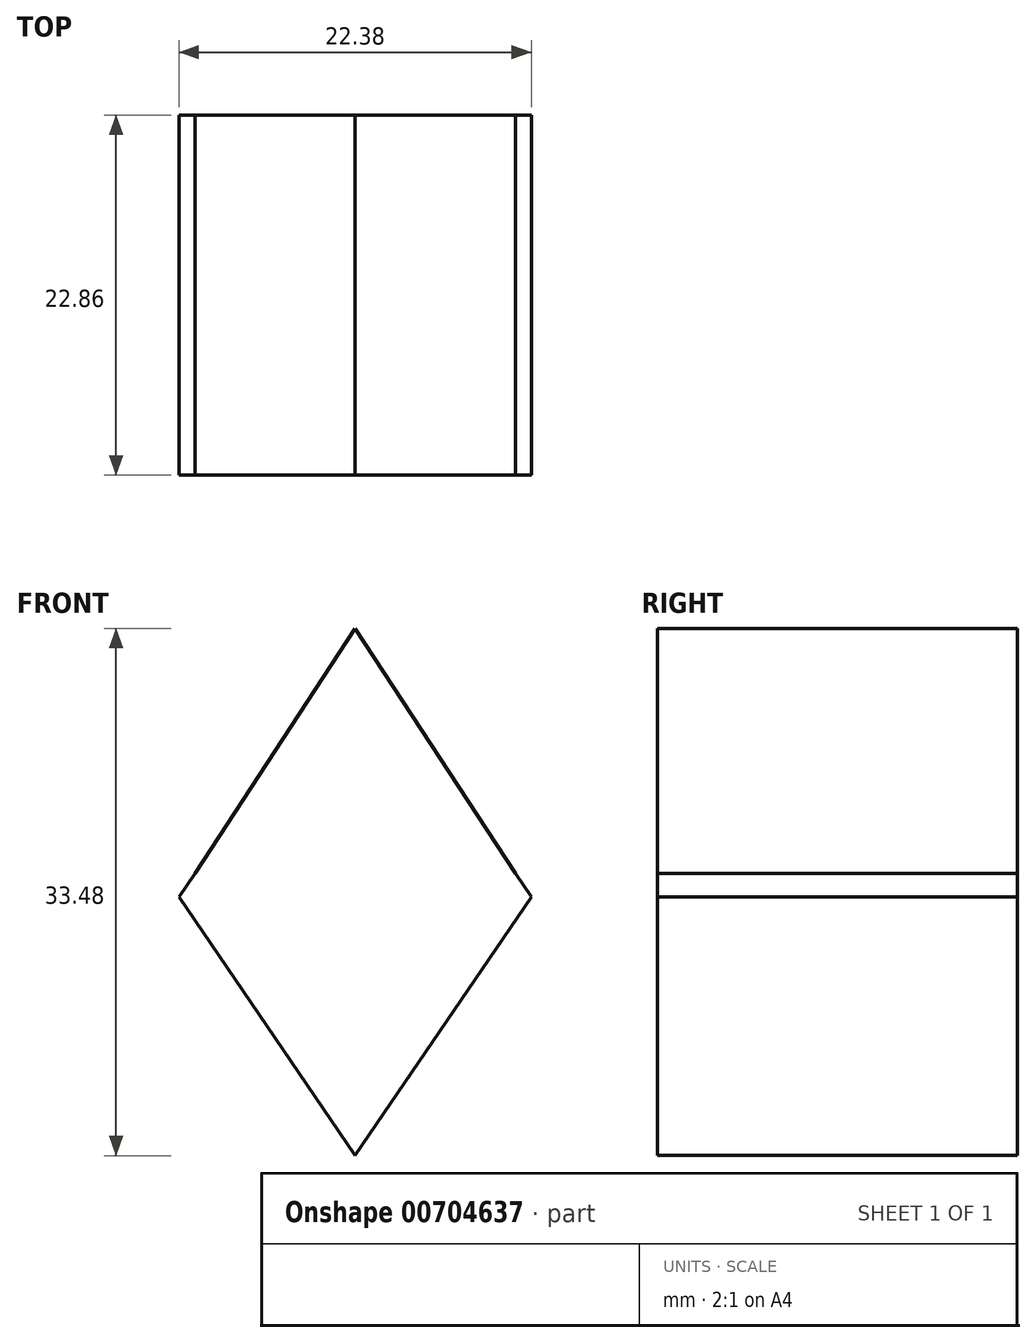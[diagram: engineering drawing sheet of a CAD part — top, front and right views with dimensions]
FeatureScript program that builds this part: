
annotation { "Feature Type Name" : "Feature", "Feature Type Description" : "" }
export const myFeature = defineFeature(function(context is Context, id is Id, definition is map)
    precondition{}
    {
        {
            var Q0;
            Q0=qCreatedBy(makeId("Front.planeOp"),FACE);
            var sketch = newSketch(context, id + "F0", { "sketchPlane" : qUnion([Q0])});
            skFitSpline(sketch, "E0", {"points": [v(-18.66, -145.03) * mm, v(-12.41, -140.25) * mm, v(-7.43, -132.73) * mm], "startDerivative": vector(13.73, 8.78) * mm, "endDerivative": vector(8.77, 15.73) * mm});
            skFitSpline(sketch, "E1", {"points": [v(0, -156.5) * mm, v(-5.42, -154.99) * mm, v(-8.85, -151.2) * mm], "startDerivative": vector(-11.5, 1.7) * mm, "endDerivative": vector(-6.16, 8.95) * mm});
            skFitSpline(sketch, "E2", {"points": [v(-6.32, -27.2) * mm, v(-15.28, -19.21) * mm, v(-26.43, -12.1) * mm, v(-37.33, -8.05) * mm], "startDerivative": vector(-25.96, 24.63) * mm, "endDerivative": vector(-33.62, 10.63) * mm});
            skFitSpline(sketch, "E3", {"points": [v(-37.33, -3.8) * mm, v(-39.84, -2.96) * mm, v(-42.51, -2.04) * mm, v(-42.5, -2) * mm], "startDerivative": vector(-4.66, 1.6) * mm, "endDerivative": vector(0.46, 0.6) * mm});
            skFitSpline(sketch, "E4", {"points": [v(-42.5, -2) * mm, v(-36.56, 4.25) * mm, v(-31.56, 12.84) * mm], "startDerivative": vector(12.98, 12.08) * mm, "endDerivative": vector(8.97, 17.54) * mm});
            skFitSpline(sketch, "E5", {"points": [v(-31.56, 12.84) * mm, v(-28.75, 11.67) * mm, v(-26.43, 10.32) * mm], "startDerivative": vector(5.62, -2.14) * mm, "endDerivative": vector(4.63, -2.93) * mm});
            skFitSpline(sketch, "E6", {"points": [v(-23.95, 12.84) * mm, v(-17.54, 8.59) * mm, v(-10.17, 1.5) * mm], "startDerivative": vector(13.82, -8.22) * mm, "endDerivative": vector(13.74, -14.33) * mm});
            skLineSegment(sketch, "E7", {"start": v(-10.17, 1.5) * mm, "end": v(0, 17.06) * mm});
            skLineSegment(sketch, "E8", {"start": v(0, 17.06) * mm, "end": v(0, 9.54) * mm});
            skLineSegment(sketch, "E9", {"start": v(0, 9.54) * mm, "end": v(0, 17.06) * mm});
            skLineSegment(sketch, "E10", {"start": v(-37.33, -3.8) * mm, "end": v(-37.33, -8.05) * mm});
            skLineSegment(sketch, "E11", {"start": v(-23.95, 12.84) * mm, "end": v(-26.43, 10.32) * mm});
            skLineSegment(sketch, "E12", {"start": v(-6.32, -27.2) * mm, "end": v(0, -29.82) * mm});
            skLineSegment(sketch, "E13", {"start": v(0, -29.82) * mm, "end": v(-6.32, -27.2) * mm});
            skLineSegment(sketch, "E14", {"start": v(-7.43, -132.73) * mm, "end": v(-4.54, -130.41) * mm});
            skLineSegment(sketch, "E15", {"start": v(-4.54, -130.41) * mm, "end": v(0, -130.41) * mm});
            skLineSegment(sketch, "E16", {"start": v(0, -130.41) * mm, "end": v(-4.54, -130.41) * mm});
            skLineSegment(sketch, "E17", {"start": v(-8.85, -151.2) * mm, "end": v(-10.72, -152.9) * mm});
            skLineSegment(sketch, "E18", {"start": v(-10.72, -152.9) * mm, "end": v(-18.24, -148.4) * mm});
            skLineSegment(sketch, "E19", {"start": v(-18.24, -148.4) * mm, "end": v(-18.66, -145.03) * mm});
            skLineSegment(sketch, "E20.MirrorCS", {"start": v(10.17, 1.5) * mm, "end": v(0, 17.06) * mm});
            skFitSpline(sketch, "E21.MirrorCS", {"points": [v(23.95, 12.84) * mm, v(17.54, 8.59) * mm, v(10.17, 1.5) * mm], "startDerivative": vector(-13.82, -8.22) * mm, "endDerivative": vector(-13.74, -14.33) * mm});
            skLineSegment(sketch, "E22.MirrorCS", {"start": v(23.95, 12.84) * mm, "end": v(26.43, 10.32) * mm});
            skFitSpline(sketch, "E23.MirrorCS", {"points": [v(31.56, 12.84) * mm, v(28.75, 11.67) * mm, v(26.43, 10.32) * mm], "startDerivative": vector(-5.62, -2.14) * mm, "endDerivative": vector(-4.63, -2.93) * mm});
            skFitSpline(sketch, "E24.MirrorCS", {"points": [v(42.5, -2) * mm, v(36.56, 4.25) * mm, v(31.56, 12.84) * mm], "startDerivative": vector(-12.98, 12.08) * mm, "endDerivative": vector(-8.97, 17.54) * mm});
            skFitSpline(sketch, "E25.MirrorCS", {"points": [v(37.33, -3.8) * mm, v(39.84, -2.96) * mm, v(42.51, -2.04) * mm, v(42.5, -2) * mm], "startDerivative": vector(4.66, 1.6) * mm, "endDerivative": vector(-0.46, 0.6) * mm});
            skLineSegment(sketch, "E26.MirrorCS", {"start": v(37.33, -3.8) * mm, "end": v(37.33, -8.05) * mm});
            skFitSpline(sketch, "E27.MirrorCS", {"points": [v(6.32, -27.2) * mm, v(15.28, -19.21) * mm, v(26.43, -12.1) * mm, v(37.33, -8.05) * mm], "startDerivative": vector(25.96, 24.63) * mm, "endDerivative": vector(33.62, 10.63) * mm});
            skLineSegment(sketch, "E28.MirrorCS", {"start": v(6.32, -27.2) * mm, "end": v(0, -29.82) * mm});
            skLineSegment(sketch, "E29.MirrorCS", {"start": v(0, -130.41) * mm, "end": v(4.54, -130.41) * mm});
            skLineSegment(sketch, "E30.MirrorCS", {"start": v(7.43, -132.73) * mm, "end": v(4.54, -130.41) * mm});
            skFitSpline(sketch, "E31.MirrorCS", {"points": [v(18.66, -145.03) * mm, v(12.41, -140.25) * mm, v(7.43, -132.73) * mm], "startDerivative": vector(-13.73, 8.78) * mm, "endDerivative": vector(-8.77, 15.73) * mm});
            skLineSegment(sketch, "E32.MirrorCS", {"start": v(18.24, -148.4) * mm, "end": v(18.66, -145.03) * mm});
            skLineSegment(sketch, "E33.MirrorCS", {"start": v(10.72, -152.9) * mm, "end": v(18.24, -148.4) * mm});
            skLineSegment(sketch, "E34.MirrorCS", {"start": v(8.85, -151.2) * mm, "end": v(10.72, -152.9) * mm});
            skFitSpline(sketch, "E35.MirrorCS", {"points": [v(0, -156.5) * mm, v(5.42, -154.99) * mm, v(8.85, -151.2) * mm], "startDerivative": vector(11.5, 1.7) * mm, "endDerivative": vector(6.16, 8.95) * mm});
            skSolve(sketch);
        }
        {
            var Q0;
            Q0=makeQuery(id+"F0.imprint","IMPRINT",FACE,{"disambiguationData":[TD([[makeQuery(id+"F0.imprint","IMPRINT",EDGE,{"derivedFrom":sQuery(id+"F0.wireOp",EDGE,"E2")}),-1.0]])]});
            var Q1;
            Q1=makeQuery(id+"F0.imprint","IMPRINT",FACE,{"disambiguationData":[TD([[makeQuery(id+"F0.imprint","IMPRINT",EDGE,{"derivedFrom":sQuery(id+"F0.wireOp",EDGE,"E0")}),-1.0]])]});
            extrude(context, id + "F1", {"entities" : qUnion([Q0, Q1]), "depth" : 6.35 * mm, "offsetDistance" : 25.4 * mm});
        }
        {
            var Q0;
            Q0=makeQuery(id+"F1.opExtrude","CAP_FACE",FACE,{"disambiguationData":[OSD([sQuery(id+"F0.wireOp",EDGE,"E2"),sQuery(id+"F0.wireOp",EDGE,"E3"),sQuery(id+"F0.wireOp",EDGE,"E4"),sQuery(id+"F0.wireOp",EDGE,"E5"),sQuery(id+"F0.wireOp",EDGE,"E6"),sQuery(id+"F0.wireOp",EDGE,"E7"),sQuery(id+"F0.wireOp",EDGE,"E10"),sQuery(id+"F0.wireOp",EDGE,"E11"),sQuery(id+"F0.wireOp",EDGE,"E13"),sQuery(id+"F0.wireOp",EDGE,"E20.MirrorCS"),sQuery(id+"F0.wireOp",EDGE,"E21.MirrorCS"),sQuery(id+"F0.wireOp",EDGE,"E22.MirrorCS"),sQuery(id+"F0.wireOp",EDGE,"E23.MirrorCS"),sQuery(id+"F0.wireOp",EDGE,"E24.MirrorCS"),sQuery(id+"F0.wireOp",EDGE,"E25.MirrorCS"),sQuery(id+"F0.wireOp",EDGE,"E26.MirrorCS"),sQuery(id+"F0.wireOp",EDGE,"E27.MirrorCS"),sQuery(id+"F0.wireOp",EDGE,"E28.MirrorCS")])],"isStart":true});
            var Q1;
            Q1=makeQuery(id+"F1.opExtrude","CAP_FACE",FACE,{"disambiguationData":[OSD([sQuery(id+"F0.wireOp",EDGE,"E0"),sQuery(id+"F0.wireOp",EDGE,"E1"),sQuery(id+"F0.wireOp",EDGE,"E14"),sQuery(id+"F0.wireOp",EDGE,"E16"),sQuery(id+"F0.wireOp",EDGE,"E17"),sQuery(id+"F0.wireOp",EDGE,"E18"),sQuery(id+"F0.wireOp",EDGE,"E19"),sQuery(id+"F0.wireOp",EDGE,"E29.MirrorCS"),sQuery(id+"F0.wireOp",EDGE,"E30.MirrorCS"),sQuery(id+"F0.wireOp",EDGE,"E31.MirrorCS"),sQuery(id+"F0.wireOp",EDGE,"E32.MirrorCS"),sQuery(id+"F0.wireOp",EDGE,"E33.MirrorCS"),sQuery(id+"F0.wireOp",EDGE,"E34.MirrorCS"),sQuery(id+"F0.wireOp",EDGE,"E35.MirrorCS")])],"isStart":true});
            extrude(context, id + "F2", {"entities" : qUnion([Q0, Q1]), "depth" : 6.35 * mm, "offsetDistance" : 25.4 * mm});
        }
        {
            var Q0;
            Q0=makeQuery(id+"F1.opExtrude","CAP_FACE",FACE,{"disambiguationData":[OSD([sQuery(id+"F0.wireOp",EDGE,"E2"),sQuery(id+"F0.wireOp",EDGE,"E3"),sQuery(id+"F0.wireOp",EDGE,"E4"),sQuery(id+"F0.wireOp",EDGE,"E5"),sQuery(id+"F0.wireOp",EDGE,"E6"),sQuery(id+"F0.wireOp",EDGE,"E7"),sQuery(id+"F0.wireOp",EDGE,"E10"),sQuery(id+"F0.wireOp",EDGE,"E11"),sQuery(id+"F0.wireOp",EDGE,"E13"),sQuery(id+"F0.wireOp",EDGE,"E20.MirrorCS"),sQuery(id+"F0.wireOp",EDGE,"E21.MirrorCS"),sQuery(id+"F0.wireOp",EDGE,"E22.MirrorCS"),sQuery(id+"F0.wireOp",EDGE,"E23.MirrorCS"),sQuery(id+"F0.wireOp",EDGE,"E24.MirrorCS"),sQuery(id+"F0.wireOp",EDGE,"E25.MirrorCS"),sQuery(id+"F0.wireOp",EDGE,"E26.MirrorCS"),sQuery(id+"F0.wireOp",EDGE,"E27.MirrorCS"),sQuery(id+"F0.wireOp",EDGE,"E28.MirrorCS")])],"isStart":false});
            var sketch = newSketch(context, id + "F3", { "sketchPlane" : qUnion([Q0])});
            skFitSpline(sketch, "E36", {"points": [v(-26.43, 10.32) * mm, v(-20.88, 7.37) * mm, v(-15.82, 3.86) * mm, v(-11.19, 0) * mm, v(-9.86, -1.24) * mm], "startDerivative": vector(19.99, -10.01) * mm, "endDerivative": vector(7.2, -6.92) * mm});
            skLineSegment(sketch, "E37", {"start": v(-9.86, -1.24) * mm, "end": v(0, -16.46) * mm});
            skLineSegment(sketch, "E38.MirrorCS", {"start": v(9.86, -1.24) * mm, "end": v(0, -16.46) * mm});
            skFitSpline(sketch, "E39.MirrorCS", {"points": [v(26.43, 10.32) * mm, v(20.88, 7.37) * mm, v(15.82, 3.86) * mm, v(11.19, 0) * mm, v(9.86, -1.24) * mm], "startDerivative": vector(-19.99, -10.01) * mm, "endDerivative": vector(-7.2, -6.92) * mm});
            skLineSegment(sketch, "E40", {"start": v(-10.17, 1.5) * mm, "end": v(-11.19, 0) * mm});
            skLineSegment(sketch, "E41", {"start": v(10.17, 1.5) * mm, "end": v(11.19, 0) * mm});
            skSolve(sketch);
        }
        {
            var Q0;
            {var subQ7=sQuery(id+"F3.wireOp",EDGE,"E37");Q0=makeQuery(id+"F3.imprint","IMPRINT",FACE,{"disambiguationData":[TD([[makeQuery(id+"F3.imprint","IMPRINT",EDGE,{"derivedFrom":subQ7}),-1.0]])]});}
            var Q1;
            {var subQ3=sQuery(id+"F3.wireOp",EDGE,"E37");Q1=makeQuery(id+"F3.imprint","IMPRINT",FACE,{"disambiguationData":[TD([[makeQuery(id+"F3.imprint","IMPRINT",EDGE,{"derivedFrom":subQ3}),1.0]])]});}
            extrude(context, id + "F4", {"entities" : qUnion([Q0, Q1]), "operationType" : NewBodyOperationType.ADD, "depth" : 2.54 * mm, "offsetDistance" : 25.4 * mm});
        }
        {
            var Q0;
            Q0=makeQuery(id+"F4.opExtrude","CAP_FACE",FACE,{"disambiguationData":[OSD([sQuery(id+"F0.wireOp",EDGE,"E2"),sQuery(id+"F0.wireOp",EDGE,"E3"),sQuery(id+"F0.wireOp",EDGE,"E4"),sQuery(id+"F0.wireOp",EDGE,"E5"),sQuery(id+"F0.wireOp",EDGE,"E7"),sQuery(id+"F0.wireOp",EDGE,"E10"),sQuery(id+"F0.wireOp",EDGE,"E13"),sQuery(id+"F0.wireOp",EDGE,"E20.MirrorCS"),sQuery(id+"F0.wireOp",EDGE,"E23.MirrorCS"),sQuery(id+"F0.wireOp",EDGE,"E24.MirrorCS"),sQuery(id+"F0.wireOp",EDGE,"E25.MirrorCS"),sQuery(id+"F0.wireOp",EDGE,"E26.MirrorCS"),sQuery(id+"F0.wireOp",EDGE,"E27.MirrorCS"),sQuery(id+"F0.wireOp",EDGE,"E28.MirrorCS"),sQuery(id+"F3.wireOp",EDGE,"E36"),sQuery(id+"F3.wireOp",EDGE,"E39.MirrorCS"),sQuery(id+"F3.wireOp",EDGE,"E40"),sQuery(id+"F3.wireOp",EDGE,"E41")])],"isStart":false});
            extrude(context, id + "F5", {"entities" : qUnion([Q0]), "oppositeDirection" : true, "depth" : 17.78 * mm, "offsetDistance" : 25.4 * mm});
        }
        {
            var Q0;
            Q0=makeQuery(id+"F5.opExtrude","CAP_FACE",FACE,{"disambiguationData":[OSD([sQuery(id+"F0.wireOp",EDGE,"E2"),sQuery(id+"F0.wireOp",EDGE,"E3"),sQuery(id+"F0.wireOp",EDGE,"E4"),sQuery(id+"F0.wireOp",EDGE,"E5"),sQuery(id+"F0.wireOp",EDGE,"E7"),sQuery(id+"F0.wireOp",EDGE,"E10"),sQuery(id+"F0.wireOp",EDGE,"E13"),sQuery(id+"F0.wireOp",EDGE,"E20.MirrorCS"),sQuery(id+"F0.wireOp",EDGE,"E23.MirrorCS"),sQuery(id+"F0.wireOp",EDGE,"E24.MirrorCS"),sQuery(id+"F0.wireOp",EDGE,"E25.MirrorCS"),sQuery(id+"F0.wireOp",EDGE,"E26.MirrorCS"),sQuery(id+"F0.wireOp",EDGE,"E27.MirrorCS"),sQuery(id+"F0.wireOp",EDGE,"E28.MirrorCS"),sQuery(id+"F3.wireOp",EDGE,"E36"),sQuery(id+"F3.wireOp",EDGE,"E39.MirrorCS"),sQuery(id+"F3.wireOp",EDGE,"E40"),sQuery(id+"F3.wireOp",EDGE,"E41")])],"isStart":true});
            var sketch = newSketch(context, id + "F6", { "sketchPlane" : qUnion([Q0])});
            skLineSegment(sketch, "E42", {"start": v(-11.19, 0) * mm, "end": v(0, -16.42) * mm});
            skLineSegment(sketch, "E43", {"start": v(0, -16.42) * mm, "end": v(11.19, 0) * mm});
            skSolve(sketch);
        }
        {
            var Q0;
            Q0=makeQuery(id+"F6.imprint","IMPRINT",FACE,{"disambiguationData":[TD([[makeQuery(id+"F6.imprint","IMPRINT",EDGE,{"derivedFrom":sQuery(id+"F6.wireOp",EDGE,"E42")}),-1.0]])]});
            var sketch = newSketch(context, id + "F7", { "sketchPlane" : qUnion([Q0])});
            skLineSegment(sketch, "E44", {"start": v(0, -16.57) * mm, "end": v(-11.35, 0) * mm});
            skLineSegment(sketch, "E45", {"start": v(-11.35, 0) * mm, "end": v(0, -16.57) * mm});
            skLineSegment(sketch, "E46.MirrorCS", {"start": v(11.35, 0) * mm, "end": v(0, -16.57) * mm});
            skSolve(sketch);
        }
        {
            var Q0;
            Q0=makeQuery(id+"F6.imprint","IMPRINT",FACE,{"disambiguationData":[TD([[makeQuery(id+"F6.imprint","IMPRINT",EDGE,{"derivedFrom":sQuery(id+"F6.wireOp",EDGE,"E42")}),1.0]])]});
            extrude(context, id + "F8", {"entities" : qUnion([Q0]), "operationType" : NewBodyOperationType.ADD, "depth" : 2.54 * mm, "offsetDistance" : 25.4 * mm});
        }
        {
            var Q0;
            Q0=makeQuery(id+"F8.opExtrude","CAP_FACE",FACE,{"disambiguationData":[OSD([sQuery(id+"F0.wireOp",EDGE,"E7"),sQuery(id+"F0.wireOp",EDGE,"E20.MirrorCS"),sQuery(id+"F3.wireOp",EDGE,"E40"),sQuery(id+"F3.wireOp",EDGE,"E41"),sQuery(id+"F6.wireOp",EDGE,"E42"),sQuery(id+"F6.wireOp",EDGE,"E43")])],"isStart":false});
            extrude(context, id + "F9", {"entities" : qUnion([Q0]), "operationType" : NewBodyOperationType.ADD, "oppositeDirection" : true, "depth" : 22.86 * mm, "offsetDistance" : 25.4 * mm});
        }
        {
            var Q0;
            Q0=makeQuery(id+"F7.imprint","IMPRINT",FACE,{"disambiguationData":[TD([[makeQuery(id+"F7.imprint","IMPRINT",EDGE,{"derivedFrom":makeQuery(id+"F6.imprint","IMPRINT",EDGE,{"derivedFrom":sQuery(id+"F6.wireOp",EDGE,"E42")})}),-1.0]])]});
            var Q1;
            {var subQ0=sQuery(id+"F0.wireOp",EDGE,"E11");var subQ1=sQuery(id+"F0.wireOp",EDGE,"E7");var subQ2=sQuery(id+"F0.wireOp",EDGE,"E6");var subQ3=sQuery(id+"F0.wireOp",EDGE,"E5");Q1=makeQuery(id+"F4.boolean.opBoolean","SPLIT",FACE,{"disambiguationData":[TD([makeQuery(id+"F1.opExtrude","SWEPT_FACE",FACE,{"disambiguationData":[OSD([subQ3])]})])],"derivedFrom":makeQuery(id+"F1.opExtrude","CAP_FACE",FACE,{"disambiguationData":[OSD([sQuery(id+"F0.wireOp",EDGE,"E2"),sQuery(id+"F0.wireOp",EDGE,"E3"),sQuery(id+"F0.wireOp",EDGE,"E4"),subQ3,subQ2,subQ1,sQuery(id+"F0.wireOp",EDGE,"E10"),subQ0,sQuery(id+"F0.wireOp",EDGE,"E13"),sQuery(id+"F0.wireOp",EDGE,"E20.MirrorCS"),sQuery(id+"F0.wireOp",EDGE,"E21.MirrorCS"),sQuery(id+"F0.wireOp",EDGE,"E22.MirrorCS"),sQuery(id+"F0.wireOp",EDGE,"E23.MirrorCS"),sQuery(id+"F0.wireOp",EDGE,"E24.MirrorCS"),sQuery(id+"F0.wireOp",EDGE,"E25.MirrorCS"),sQuery(id+"F0.wireOp",EDGE,"E26.MirrorCS"),sQuery(id+"F0.wireOp",EDGE,"E27.MirrorCS"),sQuery(id+"F0.wireOp",EDGE,"E28.MirrorCS")])],"isStart":false})});}
            var Q2;
            {var subQ0=sQuery(id+"F0.wireOp",EDGE,"E23.MirrorCS");var subQ1=sQuery(id+"F0.wireOp",EDGE,"E22.MirrorCS");var subQ2=sQuery(id+"F0.wireOp",EDGE,"E21.MirrorCS");var subQ3=sQuery(id+"F0.wireOp",EDGE,"E20.MirrorCS");Q2=makeQuery(id+"F4.boolean.opBoolean","SPLIT",FACE,{"disambiguationData":[TD([makeQuery(id+"F1.opExtrude","SWEPT_FACE",FACE,{"disambiguationData":[OSD([subQ3])]})])],"derivedFrom":makeQuery(id+"F1.opExtrude","CAP_FACE",FACE,{"disambiguationData":[OSD([sQuery(id+"F0.wireOp",EDGE,"E2"),sQuery(id+"F0.wireOp",EDGE,"E3"),sQuery(id+"F0.wireOp",EDGE,"E4"),sQuery(id+"F0.wireOp",EDGE,"E5"),sQuery(id+"F0.wireOp",EDGE,"E6"),sQuery(id+"F0.wireOp",EDGE,"E7"),sQuery(id+"F0.wireOp",EDGE,"E10"),sQuery(id+"F0.wireOp",EDGE,"E11"),sQuery(id+"F0.wireOp",EDGE,"E13"),subQ3,subQ2,subQ1,subQ0,sQuery(id+"F0.wireOp",EDGE,"E24.MirrorCS"),sQuery(id+"F0.wireOp",EDGE,"E25.MirrorCS"),sQuery(id+"F0.wireOp",EDGE,"E26.MirrorCS"),sQuery(id+"F0.wireOp",EDGE,"E27.MirrorCS"),sQuery(id+"F0.wireOp",EDGE,"E28.MirrorCS")])],"isStart":false})});}
            extrude(context, id + "F10", {"entities" : qUnion([Q0, Q1, Q2]), "operationType" : NewBodyOperationType.REMOVE, "oppositeDirection" : true, "depth" : 25.4 * mm, "offsetDistance" : 25.4 * mm});
        }
        {
            var Q0;
            Q0=makeQuery(id+"F1.opExtrude","CAP_FACE",FACE,{"disambiguationData":[OSD([sQuery(id+"F0.wireOp",EDGE,"E0"),sQuery(id+"F0.wireOp",EDGE,"E1"),sQuery(id+"F0.wireOp",EDGE,"E14"),sQuery(id+"F0.wireOp",EDGE,"E16"),sQuery(id+"F0.wireOp",EDGE,"E17"),sQuery(id+"F0.wireOp",EDGE,"E18"),sQuery(id+"F0.wireOp",EDGE,"E19"),sQuery(id+"F0.wireOp",EDGE,"E29.MirrorCS"),sQuery(id+"F0.wireOp",EDGE,"E30.MirrorCS"),sQuery(id+"F0.wireOp",EDGE,"E31.MirrorCS"),sQuery(id+"F0.wireOp",EDGE,"E32.MirrorCS"),sQuery(id+"F0.wireOp",EDGE,"E33.MirrorCS"),sQuery(id+"F0.wireOp",EDGE,"E34.MirrorCS"),sQuery(id+"F0.wireOp",EDGE,"E35.MirrorCS")])],"isStart":false});
            extrude(context, id + "F11", {"entities" : qUnion([Q0]), "operationType" : NewBodyOperationType.REMOVE, "oppositeDirection" : true, "depth" : 25.4 * mm, "offsetDistance" : 25.4 * mm});
        }
    });
